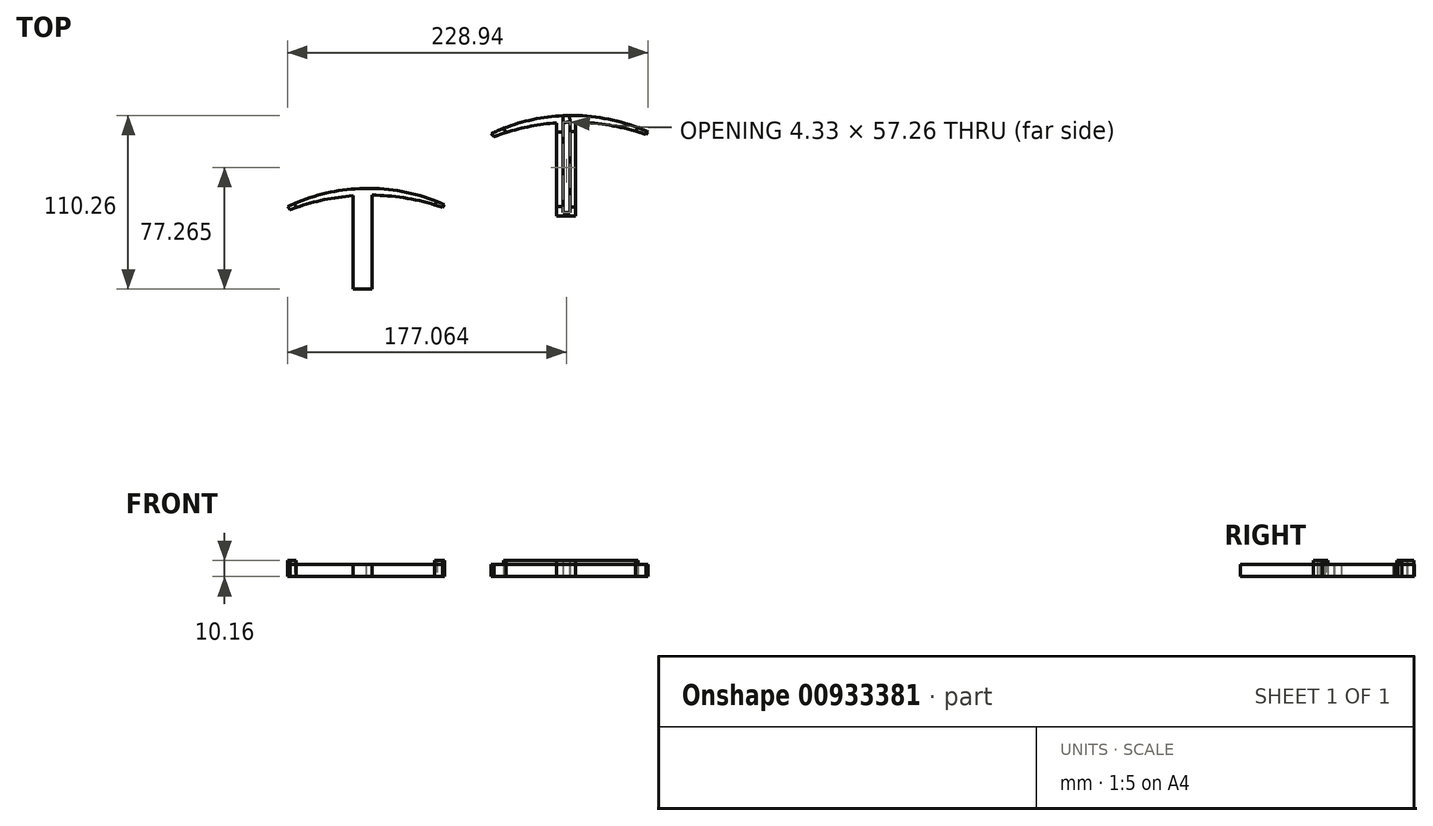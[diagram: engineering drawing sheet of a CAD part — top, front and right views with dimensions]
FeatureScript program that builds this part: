
annotation { "Feature Type Name" : "Feature", "Feature Type Description" : "" }
export const myFeature = defineFeature(function(context is Context, id is Id, definition is map)
    precondition{}
    {
        {
            var Q0;
            Q0=qCreatedBy(makeId("Top.planeOp"),FACE);
            var sketch = newSketch(context, id + "F0", { "sketchPlane" : qUnion([Q0])});
            skArc(sketch, "E0", {"start": v(31.49, 8.67) * mm, "mid": v(-18.5, 19.06) * mm, "end": v(-68.2, 7.47) * mm});
            skArc(sketch, "E1", {"start": v(30.29, 6.95) * mm, "mid": v(-18.22, 14.77) * mm, "end": v(-66.49, 5.58) * mm});
            skLineSegment(sketch, "E2", {"start": v(-68.2, 7.47) * mm, "end": v(-66.49, 5.58) * mm});
            skLineSegment(sketch, "E3", {"start": v(31.49, 8.67) * mm, "end": v(30.29, 6.95) * mm});
            skLineSegment(sketch, "E4", {"start": v(-63.86, 9.44) * mm, "end": v(-62.7, 6.95) * mm});
            skLineSegment(sketch, "E5", {"start": v(-60.17, 10.95) * mm, "end": v(-58.86, 8.23) * mm});
            skLineSegment(sketch, "E6", {"start": v(24.96, 11.37) * mm, "end": v(23.42, 9.14) * mm});
            skLineSegment(sketch, "E7", {"start": v(26.83, 10.64) * mm, "end": v(25.25, 8.6) * mm});
            skLineSegment(sketch, "E8", {"start": v(-26.77, 14.39) * mm, "end": v(-26.77, -44.8) * mm});
            skLineSegment(sketch, "E9", {"start": v(-26.77, -44.8) * mm, "end": v(-14.7, -44.8) * mm});
            skLineSegment(sketch, "E10", {"start": v(-14.7, -44.8) * mm, "end": v(-14.7, 14.77) * mm});
            skLineSegment(sketch, "E11", {"start": v(-22.56, 14.64) * mm, "end": v(-22.56, -42.5) * mm});
            skLineSegment(sketch, "E12", {"start": v(-22.56, -42.5) * mm, "end": v(-18.23, -42.5) * mm});
            skLineSegment(sketch, "E13", {"start": v(-18.23, -42.5) * mm, "end": v(-18.23, 14.77) * mm});
            skLineSegment(sketch, "E14", {"start": v(-22.56, 14.64) * mm, "end": v(-22.56, 18.94) * mm});
            skLineSegment(sketch, "E15", {"start": v(-22.56, 18.94) * mm, "end": v(-18.5, 19.13) * mm});
            skPoint(sketch, "E15.endSnap0", {"position": v(-18.5, 19.06) * mm});
            skLineSegment(sketch, "E16", {"start": v(-18.5, 19.13) * mm, "end": v(-18.23, 14.77) * mm});
            skArc(sketch, "E17", {"start": v(160.74, 54.98) * mm, "mid": v(110.77, 65.38) * mm, "end": v(61.06, 53.78) * mm});
            skArc(sketch, "E18", {"start": v(159.54, 53.27) * mm, "mid": v(111.04, 61.08) * mm, "end": v(62.77, 51.9) * mm});
            skLineSegment(sketch, "E19", {"start": v(61.06, 53.78) * mm, "end": v(62.77, 51.9) * mm});
            skLineSegment(sketch, "E20", {"start": v(160.74, 54.98) * mm, "end": v(159.54, 53.27) * mm});
            skLineSegment(sketch, "E21", {"start": v(65.4, 55.76) * mm, "end": v(66.55, 53.27) * mm});
            skLineSegment(sketch, "E22", {"start": v(69.08, 57.27) * mm, "end": v(70.4, 54.54) * mm});
            skLineSegment(sketch, "E23", {"start": v(154.22, 57.68) * mm, "end": v(152.68, 55.46) * mm});
            skLineSegment(sketch, "E24", {"start": v(156.09, 56.96) * mm, "end": v(154.5, 54.91) * mm});
            skLineSegment(sketch, "E25", {"start": v(102.48, 60.7) * mm, "end": v(102.48, 1.5) * mm});
            skLineSegment(sketch, "E26", {"start": v(102.48, 1.5) * mm, "end": v(114.56, 1.5) * mm});
            skLineSegment(sketch, "E27", {"start": v(114.56, 1.5) * mm, "end": v(114.56, 61.1) * mm});
            skLineSegment(sketch, "E28", {"start": v(106.7, 60.96) * mm, "end": v(106.7, 3.83) * mm});
            skLineSegment(sketch, "E29", {"start": v(106.7, 3.83) * mm, "end": v(111.03, 3.83) * mm});
            skLineSegment(sketch, "E30", {"start": v(111.03, 3.83) * mm, "end": v(111.03, 61.08) * mm});
            skLineSegment(sketch, "E31", {"start": v(106.7, 60.96) * mm, "end": v(106.7, 65.26) * mm});
            skLineSegment(sketch, "E32", {"start": v(106.7, 65.26) * mm, "end": v(110.77, 65.45) * mm});
            skPoint(sketch, "E32.endSnap0", {"position": v(110.77, 65.38) * mm});
            skLineSegment(sketch, "E33", {"start": v(110.77, 65.45) * mm, "end": v(111.03, 61.08) * mm});
            skLineSegment(sketch, "E34", {"start": v(102.48, 54.93) * mm, "end": v(106.7, 54.93) * mm});
            skLineSegment(sketch, "E35", {"start": v(102.48, 7.48) * mm, "end": v(106.7, 7.48) * mm});
            skLineSegment(sketch, "E36", {"start": v(111.03, 7.3) * mm, "end": v(114.56, 7.3) * mm});
            skLineSegment(sketch, "E37", {"start": v(111.03, 55.01) * mm, "end": v(114.56, 55.01) * mm});
            skSolve(sketch);
        }
        {
            var Q0;
            {var subQ0=sQuery(id+"F0.wireOp",EDGE,"E2");Q0=makeQuery(id+"F0.imprint","IMPRINT",FACE,{"disambiguationData":[TD([[makeQuery(id+"F0.imprint","IMPRINT",EDGE,{"derivedFrom":subQ0}),1.0]])]});}
            var Q1;
            {var subQ0=sQuery(id+"F0.wireOp",EDGE,"E3");Q1=makeQuery(id+"F0.imprint","IMPRINT",FACE,{"disambiguationData":[TD([[makeQuery(id+"F0.imprint","IMPRINT",EDGE,{"derivedFrom":subQ0}),-1.0]])]});}
            var Q2;
            {var subQ0=sQuery(id+"F0.wireOp",EDGE,"E22");Q2=makeQuery(id+"F0.imprint","IMPRINT",FACE,{"disambiguationData":[TD([[makeQuery(id+"F0.imprint","IMPRINT",EDGE,{"derivedFrom":subQ0}),1.0]])]});}
            var Q3;
            {var subQ0=sQuery(id+"F0.wireOp",EDGE,"E23");Q3=makeQuery(id+"F0.imprint","IMPRINT",FACE,{"disambiguationData":[TD([[makeQuery(id+"F0.imprint","IMPRINT",EDGE,{"derivedFrom":subQ0}),-1.0]])]});}
            var Q4;
            {var subQ5=sQuery(id+"F0.wireOp",EDGE,"E37");Q4=makeQuery(id+"F0.imprint","IMPRINT",FACE,{"disambiguationData":[TD([[makeQuery(id+"F0.imprint","IMPRINT",EDGE,{"derivedFrom":subQ5}),1.0]])]});}
            var Q5;
            {var subQ5=sQuery(id+"F0.wireOp",EDGE,"E34");Q5=makeQuery(id+"F0.imprint","IMPRINT",FACE,{"disambiguationData":[TD([[makeQuery(id+"F0.imprint","IMPRINT",EDGE,{"derivedFrom":subQ5}),1.0]])]});}
            var Q6;
            {var subQ5=sQuery(id+"F0.wireOp",EDGE,"E26");Q6=makeQuery(id+"F0.imprint","IMPRINT",FACE,{"disambiguationData":[TD([[makeQuery(id+"F0.imprint","IMPRINT",EDGE,{"derivedFrom":subQ5}),1.0]])]});}
            extrude(context, id + "F1", {"entities" : qUnion([Q0, Q1, Q2, Q3, Q4, Q5, Q6]), "depth" : 10.16 * mm, "offsetDistance" : 25.4 * mm});
        }
        {
            var Q0;
            Q0 = qSketchRegion(id + "F0", true);
            var Q1;
            {var subQ0=sQuery(id+"F0.wireOp",EDGE,"E11");Q1=makeQuery(id+"F0.imprint","IMPRINT",FACE,{"disambiguationData":[TD([[makeQuery(id+"F0.imprint","IMPRINT",EDGE,{"derivedFrom":subQ0}),1.0]])]});}
            extrude(context, id + "F2", {"entities" : qUnion([Q0, Q1]), "depth" : 7.62 * mm, "offsetDistance" : 25.4 * mm});
        }
    });
